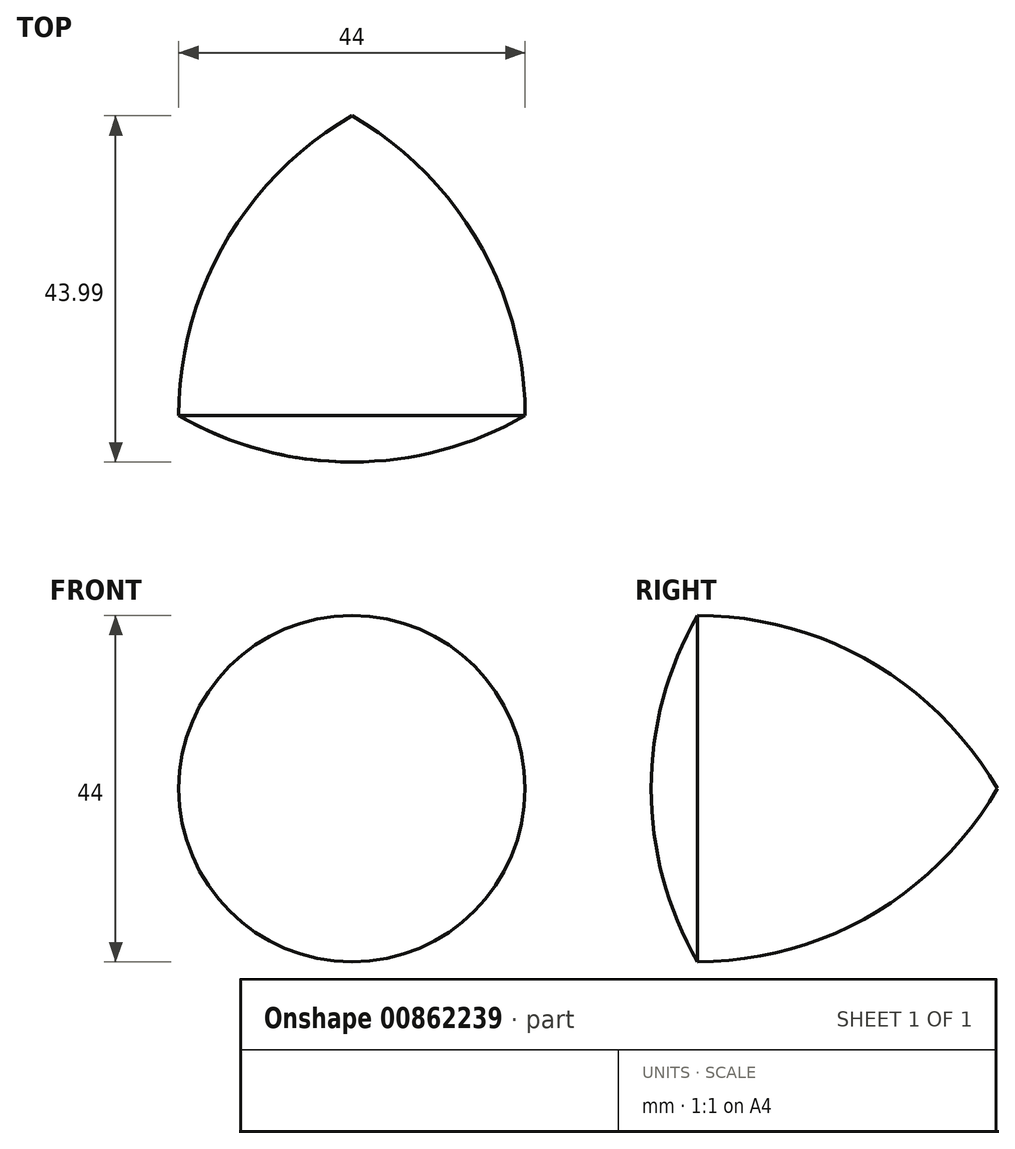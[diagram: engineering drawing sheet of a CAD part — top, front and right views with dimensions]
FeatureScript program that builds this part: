
annotation { "Feature Type Name" : "Feature", "Feature Type Description" : "" }
export const myFeature = defineFeature(function(context is Context, id is Id, definition is map)
    precondition{}
    {
        {
            var Q0;
            Q0=qCreatedBy(makeId("Top.planeOp"),FACE);
            var sketch = newSketch(context, id + "F0", { "sketchPlane" : qUnion([Q0])});
            skLineSegment(sketch, "E0.0", {"start": v(0, 25.4) * mm, "end": v(22, -12.7) * mm});
            skLineSegment(sketch, "E0.1", {"start": v(22, -12.7) * mm, "end": v(-22, -12.7) * mm});
            skLineSegment(sketch, "E0.2", {"start": v(-22, -12.7) * mm, "end": v(0, 25.4) * mm});
            skArc(sketch, "E1", {"start": v(-22, -12.7) * mm, "mid": v(0, -18.6) * mm, "end": v(22, -12.7) * mm});
            skArc(sketch, "E2", {"start": v(0, 25.4) * mm, "mid": v(-16.1, 9.3) * mm, "end": v(-22, -12.7) * mm});
            skArc(sketch, "E3", {"start": v(22, -12.7) * mm, "mid": v(16.1, 9.3) * mm, "end": v(0, 25.4) * mm});
            skLineSegment(sketch, "E4", {"start": v(0, 25.4) * mm, "end": v(0, -25.4) * mm});
            skSolve(sketch);
        }
        {
            var Q0;
            {var subQ0=sQuery(id+"F0.wireOp",EDGE,"E0.0");Q0=makeQuery(id+"F0.imprint","IMPRINT",FACE,{"disambiguationData":[TD([[makeQuery(id+"F0.imprint","IMPRINT",EDGE,{"derivedFrom":subQ0}),-1.0]])]});}
            var Q1;
            Q1=makeQuery(id+"F0.imprint","IMPRINT",FACE,{"disambiguationData":[TD([[makeQuery(id+"F0.imprint","IMPRINT",EDGE,{"derivedFrom":sQuery(id+"F0.wireOp",EDGE,"E0.0")}),1.0]])]});
            var Q2;
            {var subQ0=sQuery(id+"F0.wireOp",EDGE,"E1");var subQ3=sQuery(id+"F0.wireOp",EDGE,"E4");var subQ5=makeQuery(id+"F0.imprint","INTERSECT",VERTEX,{"derivedFrom":[subQ0,subQ3]});Q2=makeQuery(id+"F0.imprint","IMPRINT",FACE,{"disambiguationData":[TD([[makeQuery(id+"F0.imprint","IMPRINT",EDGE,{"disambiguationData":[TD([[subQ5,1.0]])],"derivedFrom":subQ3}),1.0]])]});}
            var Q3;
            Q3=sQuery(id+"F0.wireOp",EDGE,"E4");
            revolve(context, id + "F1", {"surfaceOperationType" : NewSurfaceOperationType.NEW, "entities" : qUnion([Q0, Q1, Q2]), "axis" : qUnion([Q3]), "revolveType" : RevolveType.FULL});
        }
    });
